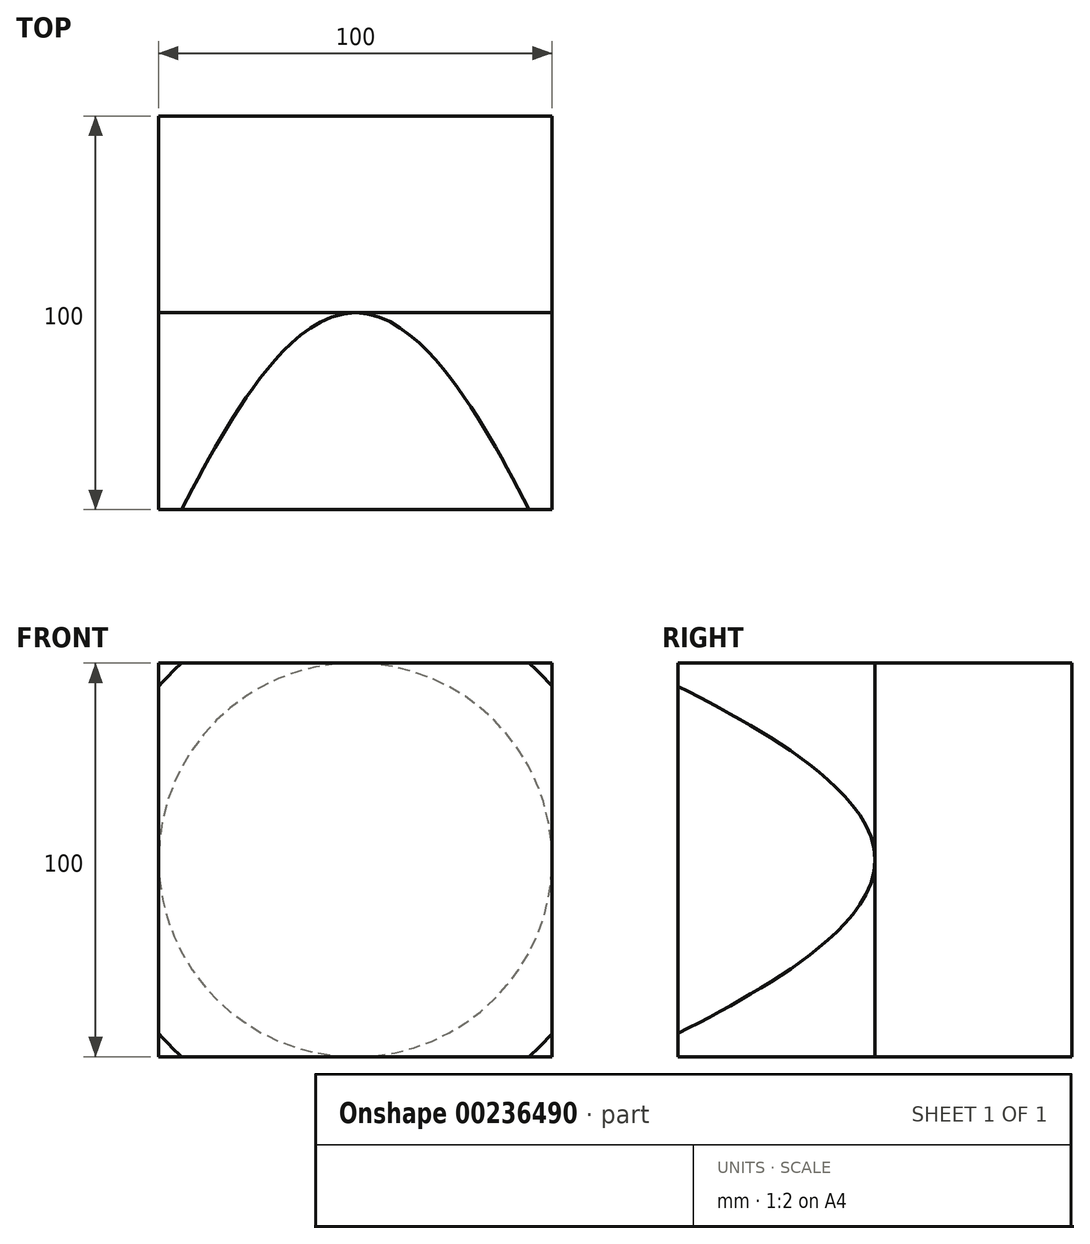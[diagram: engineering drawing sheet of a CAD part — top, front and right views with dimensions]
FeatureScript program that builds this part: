
annotation { "Feature Type Name" : "Feature", "Feature Type Description" : "" }
export const myFeature = defineFeature(function(context is Context, id is Id, definition is map)
    precondition{}
    {
        {
            var Q0;
            Q0=qCreatedBy(makeId("Top.planeOp"),FACE);
            var sketch = newSketch(context, id + "F0", { "sketchPlane" : qUnion([Q0])});
            skLineSegment(sketch, "E0.bottom", {"start": v(-50, 50) * mm, "end": v(50, 50) * mm});
            skLineSegment(sketch, "E0.top", {"start": v(-50, -50) * mm, "end": v(50, -50) * mm});
            skLineSegment(sketch, "E0.left", {"start": v(-50, 50) * mm, "end": v(-50, -50) * mm});
            skLineSegment(sketch, "E0.right", {"start": v(50, 50) * mm, "end": v(50, -50) * mm});
            skPoint(sketch, "E0.middle", {"position": v(0, 0) * mm});
            skSolve(sketch);
        }
        {
            var Q0;
            Q0=makeQuery(id+"F0.imprint","IMPRINT",FACE,{"disambiguationData":[TD([[makeQuery(id+"F0.imprint","IMPRINT",EDGE,{"derivedFrom":sQuery(id+"F0.wireOp",EDGE,"E0.bottom")}),-1.0]])]});
            extrude(context, id + "F1", {"entities" : qUnion([Q0]), "endBound" : BoundingType.SYMMETRIC, "depth" : 100 * mm});
        }
        {
            var Q0;
            Q0=qCreatedBy(makeId("Top.planeOp"),FACE);
            var sketch = newSketch(context, id + "F2", { "sketchPlane" : qUnion([Q0])});
            skLineSegment(sketch, "E1", {"start": v(50, 0) * mm, "end": v(75, 0) * mm});
            skLineSegment(sketch, "E2", {"start": v(75, 0) * mm, "end": v(75, -75) * mm});
            skLineSegment(sketch, "E3", {"start": v(75, 0) * mm, "end": v(50, 0) * mm});
            skLineSegment(sketch, "E4", {"start": v(50, 0) * mm, "end": v(75, -75) * mm});
            skLineSegment(sketch, "E5", {"start": v(0, 0) * mm, "end": v(0, -75) * mm});
            skSolve(sketch);
        }
        {
            var Q0;
            Q0=makeQuery(id+"F2.imprint","IMPRINT",FACE,{"disambiguationData":[TD([[makeQuery(id+"F2.imprint","IMPRINT",EDGE,{"derivedFrom":sQuery(id+"F2.wireOp",EDGE,"E2")}),-1.0]])]});
            var Q1;
            Q1=sQuery(id+"F2.wireOp",EDGE,"E5");
            revolve(context, id + "F3", {"operationType" : NewBodyOperationType.REMOVE, "entities" : qUnion([Q0]), "axis" : qUnion([Q1]), "revolveType" : RevolveType.FULL, "oppositeDirection" : true});
        }
    });
